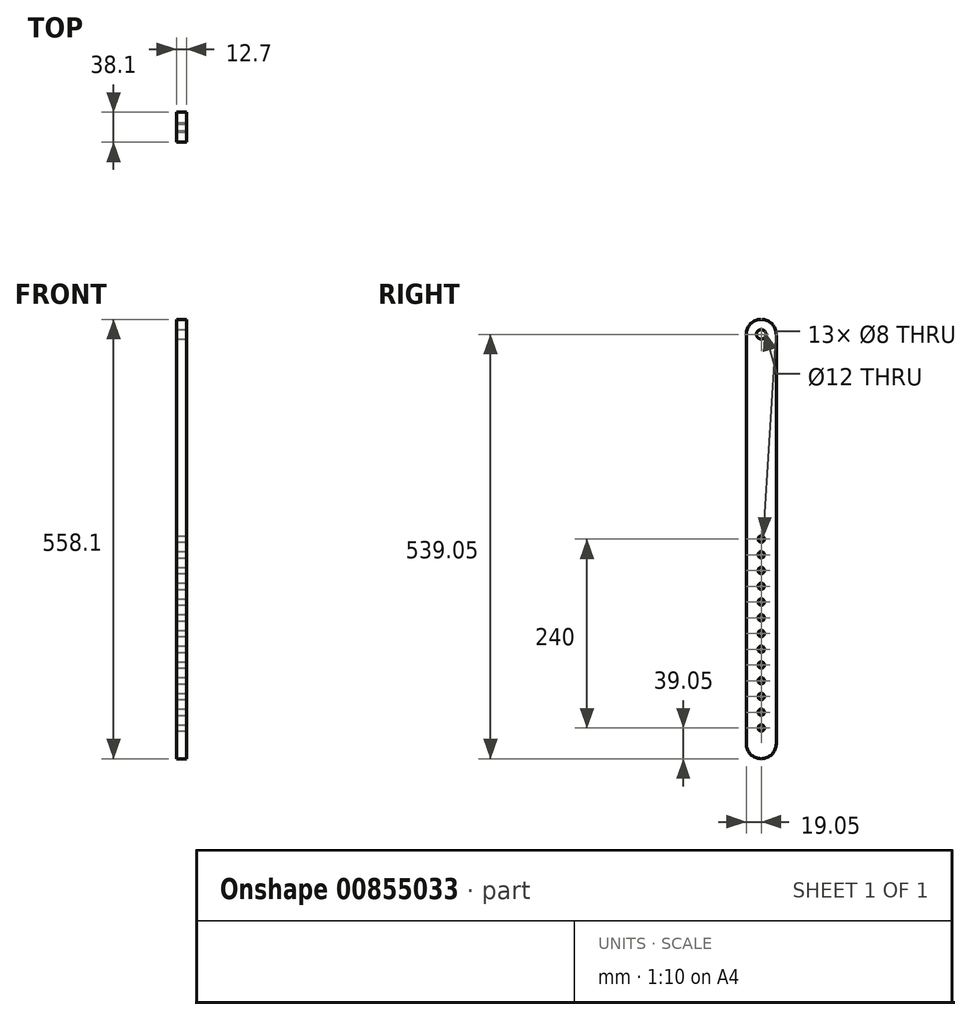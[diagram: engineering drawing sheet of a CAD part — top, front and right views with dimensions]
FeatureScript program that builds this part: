
annotation { "Feature Type Name" : "Feature", "Feature Type Description" : "" }
export const myFeature = defineFeature(function(context is Context, id is Id, definition is map)
    precondition{}
    {
        {
            var Q0;
            Q0=qCreatedBy(makeId("Right.planeOp"),FACE);
            var sketch = newSketch(context, id + "F0", { "sketchPlane" : qUnion([Q0])});
            skLineSegment(sketch, "E0", {"start": v(-19.05, 260) * mm, "end": v(-19.05, -260) * mm});
            skLineSegment(sketch, "E1", {"start": v(0, 54.22) * mm, "end": v(0, -50.31) * mm, "construction": true});
            skLineSegment(sketch, "E2.MirrorCS", {"start": v(19.05, 260) * mm, "end": v(19.05, -260) * mm});
            skArc(sketch, "E3", {"start": v(19.05, 260) * mm, "mid": v(0, 279.05) * mm, "end": v(-19.05, 260) * mm});
            skArc(sketch, "E4", {"start": v(-19.05, -260) * mm, "mid": v(0, -279.05) * mm, "end": v(19.05, -260) * mm});
            skLineSegment(sketch, "E5", {"start": v(-19.05, 0) * mm, "end": v(19.05, 0) * mm, "construction": true});
            skCircle(sketch, "E6", {"center": v(0, 260) * mm, "radius": 6 * mm});
            skCircle(sketch, "E7", {"center": v(0, 0) * mm, "radius": 4 * mm});
            skCircle(sketch, "E8.0.1.0", {"center": v(0, -20) * mm, "radius": 4 * mm});
            skCircle(sketch, "E8.0.2.0", {"center": v(0, -40) * mm, "radius": 4 * mm});
            skCircle(sketch, "E8.0.3.0", {"center": v(0, -60) * mm, "radius": 4 * mm});
            skCircle(sketch, "E8.0.4.0", {"center": v(0, -80) * mm, "radius": 4 * mm});
            skCircle(sketch, "E8.0.5.0", {"center": v(0, -100) * mm, "radius": 4 * mm});
            skCircle(sketch, "E8.0.6.0", {"center": v(0, -120) * mm, "radius": 4 * mm});
            skCircle(sketch, "E8.0.7.0", {"center": v(0, -140) * mm, "radius": 4 * mm});
            skCircle(sketch, "E8.0.8.0", {"center": v(0, -160) * mm, "radius": 4 * mm});
            skCircle(sketch, "E8.0.9.0", {"center": v(0, -180) * mm, "radius": 4 * mm});
            skCircle(sketch, "E8.0.10.0", {"center": v(0, -200) * mm, "radius": 4 * mm});
            skCircle(sketch, "E8.0.11.0", {"center": v(0, -220) * mm, "radius": 4 * mm});
            skCircle(sketch, "E8.0.12.0", {"center": v(0, -240) * mm, "radius": 4 * mm});
            skLineSegment(sketch, "E8.direction1", {"start": v(0, 0) * mm, "end": v(25, 0) * mm, "construction": true});
            skLineSegment(sketch, "E8.direction2", {"start": v(0, 0) * mm, "end": v(0, -20) * mm, "construction": true});
            skSolve(sketch);
        }
        {
            var Q0;
            Q0=qSketchRegion(id+"F0",true);
            extrude(context, id + "F1", {"entities" : qUnion([Q0]), "oppositeDirection" : true, "depth" : 12.7 * mm, "offsetDistance" : 25 * mm});
        }
    });
